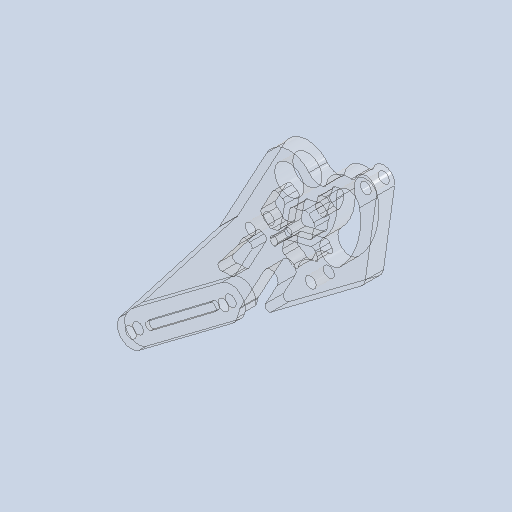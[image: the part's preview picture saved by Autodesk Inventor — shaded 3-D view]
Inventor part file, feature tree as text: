
AUTODESK INVENTOR PART (.ipt)
format: ipt  version: 2023 (Build 270158030, 158C)  size: 1,397,760 bytes
history: native  units: mm
features: extrude x27, sketch x25, projected_geometry x20, fillet x9, other x7, hole x2
ambient origin geometry x8: Origin, YZ Plane, XZ Plane, XY Plane, X Axis, Y Axis, Z Axis, Center Point
bodies: Body1 (feature_tree)
feature tree (90):
  other  "ソリッド1"
  sketch  "スケッチ1"
  sketch  "スケッチ2"
  extrude  "押し出し1"  Depth=5.0mm TaperAngle=0.0deg
  hole  "穴1"  [1 undecoded]
  fillet  "フィレット1"  Radius=4.0mm
  extrude  "押し出し2"  Depth=5.0mm TaperAngle=0.0deg
  extrude  "押し出し3"  Depth=10.0mm TaperAngle=0.0deg
  extrude  "押し出し4"  Depth=1.0mm TaperAngle=0.0deg
  extrude  "押し出し5"  Depth=4.014257mm
  sketch  "スケッチ7"
  extrude  "押し出し6"  Depth=7.971681mm
  extrude  "押し出し7"  Depth=3.98584mm
  extrude  "押し出し8"  Depth=2.0mm TaperAngle=0.0deg
  extrude  "押し出し9"  Depth=4.0mm TaperAngle=0.0deg
  extrude  "押し出し10"  Depth=10.0mm TaperAngle=0.0deg
  extrude  "押し出し11"  Depth=2.0mm TaperAngle=0.0deg
  extrude  "押し出し12"  Depth=4.0mm TaperAngle=0.0deg
  sketch  "スケッチ12"
  extrude  "押し出し13"  Depth=2.0mm TaperAngle=0.0deg
  hole  "穴2"  [1 undecoded]
  extrude  "押し出し14"  Depth=6.5mm
  fillet  "フィレット2"  Radius=10.0mm
  extrude  "押し出し15"  Depth=16.0mm
  fillet  "フィレット3"  Radius=7.0mm
  extrude  "押し出し16"  Depth=8.0mm TaperAngle=0.0deg
  extrude  "押し出し17"  Depth=5.0mm
  fillet  "フィレット4"  Radius=5.0mm
  sketch  "スケッチ17"
  sketch  "スケッチ18"
  extrude  "押し出し18"  Depth=3.0mm
  extrude  "押し出し19"  Depth=3.0mm
  extrude  "押し出し20"  Depth=3.0mm
  extrude  "押し出し21"  Depth=2.0mm
  extrude  "押し出し22"  Depth=2.0mm
  sketch  "スケッチ22"
  extrude  "押し出し23"  Depth=7.0mm TaperAngle=0.0deg
  extrude  "押し出し24"  Depth=1.0mm
  extrude  "押し出し25"  Depth=3.0mm
  fillet  "フィレット5"  Radius=3.0mm
  fillet  "フィレット6"  Radius=8.0mm
  fillet  "フィレット7"  Radius=1.0mm
  fillet  "フィレット8"  Radius=8.0mm
  extrude  "押し出し26"  Depth=2.0mm
  fillet  "フィレット9"  Radius=3.0mm
  sketch  "スケッチ24"
  extrude  "押し出し27"  Depth=3.0mm TaperAngle=0.0deg
  sketch  "スケッチ3"
  projected_geometry  "投影ループ1"
  sketch  "スケッチ4"
  projected_geometry  "投影ループ2"
  sketch  "スケッチ5"
  projected_geometry  "投影ループ3"
  sketch  "スケッチ6"
  projected_geometry  "投影ループ4"
  projected_geometry  "投影ループ5"
  sketch  "スケッチ8"
  projected_geometry  "投影ループ6"
  sketch  "スケッチ9"
  projected_geometry  "投影ループ7"
  sketch  "スケッチ10"
  projected_geometry  "投影ループ8"
  sketch  "スケッチ11"
  sketch  "スケッチ13"
  projected_geometry  "投影ループ9"
  sketch  "スケッチ14"
  projected_geometry  "投影ループ10"
  sketch  "スケッチ15"
  projected_geometry  "投影ループ11"
  sketch  "スケッチ16"
  projected_geometry  "投影ループ12"
  projected_geometry  "投影ループ13"
  projected_geometry  "投影ループ14"
  projected_geometry  "投影ループ15"
  sketch  "スケッチ19"
  sketch  "スケッチ20"
  sketch  "スケッチ21"
  projected_geometry  "投影ループ16"
  projected_geometry  "投影ループ17"
  sketch  "スケッチ23"
  projected_geometry  "投影ループ18"
  projected_geometry  "投影ループ19"
  projected_geometry  "投影ループ20"
  sketch  "スケッチ25"
  other  "断面エッジを投影1"
  other  "断面エッジを投影2"
  other  "断面エッジを投影3"
  other  "断面エッジを投影4"
  other  "断面エッジを投影5"
  other  "断面エッジを投影6"
note: 2 required parameter values undecoded (feature->parameter linkage not recoverable at this tier; creation-order binding heuristic only, values carry confidence <= 0.55)
